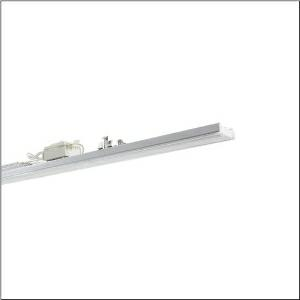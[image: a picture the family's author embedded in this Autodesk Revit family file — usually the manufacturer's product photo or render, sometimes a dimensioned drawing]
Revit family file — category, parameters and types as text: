
# Revit family: licross_r__11_recessed_mo_51tl12cn44xg_a92d
name_source: partatom
category: Lighting Fixtures
units: mm (PartAtom-declared; Revit-internal decimal feet)

## family parameters
Cut with Voids When Loaded = No
Host = Face
Light Source = No
Part Type = Normal
Room Calculation Point = No
Round Connector Dimension = Use Diameter
Shared = No

## types (1)
- Licross® 11 Recessed MO (1 x LED, 4300 lm, 21.9 W, 4000K)
    Apparent Load = 22 VA
    CIE Flux Codes = 67 92 99 100 100
    Color Rendering = 80
    Color Temperature = 4000K
    Default Elevation = 1800 mm
    Description = Licross® 11 Recessed MO, luminaire insert, of sheet steel, coil coated, white, length: 1.500mm, width: 66mm, height: 67mm, LED rated luminous flux: 4.300lm, light colour: 840, control gear: ON/OFF, CLOi, with plug, 3-pole, with phase selection, mains connection: 220..240V, AC, 50/60Hz, start of lifetime: 22W, end of service life: 24W, internal wiring halogen-free, primary optical cover: cover, of PMMA, light emission: direct distribution, primary light characteristic: symmetric, protection rating (complete): IP40, insulation class (complete): insulation class I (protective earthing), certification: CE, ENEC, VDE, UKCA, protection symbol: D if used in an environment without relevant dust loads with corresponding accessories, impact resistance: IK06, permissible ambient temperature for indoor applications: -35..+50°C, corresponds to IFS (International Featured Standards) requirements for safety and quality in the food industry, reducing of maximum allowable ambient temperature of 5°C with ceiling mounting, LABS conformity tested according to VDMA 24364:2018-05, packaging unit: 1 piece
    Height = 58 mm
    Lamp = 1 x LED
    Lamp Light Flux = 4300 lm
    Lamp Power = 21.9 W
    Lamp count = 1
    Length = 1500 mm
    Luminous efficacy = 196 lm/W
    Manufacturer = Siteco
    ModVariant = No
    Model = 51TL12CN44XG
    Mounting Place = Ceiling
    Mounting Type = Pendant
    Number of Poles = 1
    OnlyDefault = Yes
    Power Factor = 1
    Product Name = Licross® 11 Recessed MO
    Product group = luminaire insert | ceiling pendant
    ProductGroupID = 902
    Protection Class = Protection class I
    Protection Degree = IP 40
    RLX_Detail_Level = 1
    RLX_Emergency_Light_Flux = 0 lm
    RLX_Emergency_Type = 0
    RLX_Emergency_Type_DB = No
    RlxData = <blob elided: 20857 chars, md5=82d7ab02>
    Socket = socket
    Standby Power = 0 W
    System Light Flux = 4300 lm
    System Power = 22 W
    Type Comments = Product without accessories
    Type Image = l_1296930.jpg
    URL = http://relux.com
    VarID = ---
    Voltage = 0 V
    Weight = 0.00 kg
    Width = 66 mm

## geometry (parser evidence)
native form markers: Blend x4, Sweep x13
no freeform markers — native parametric forms only
